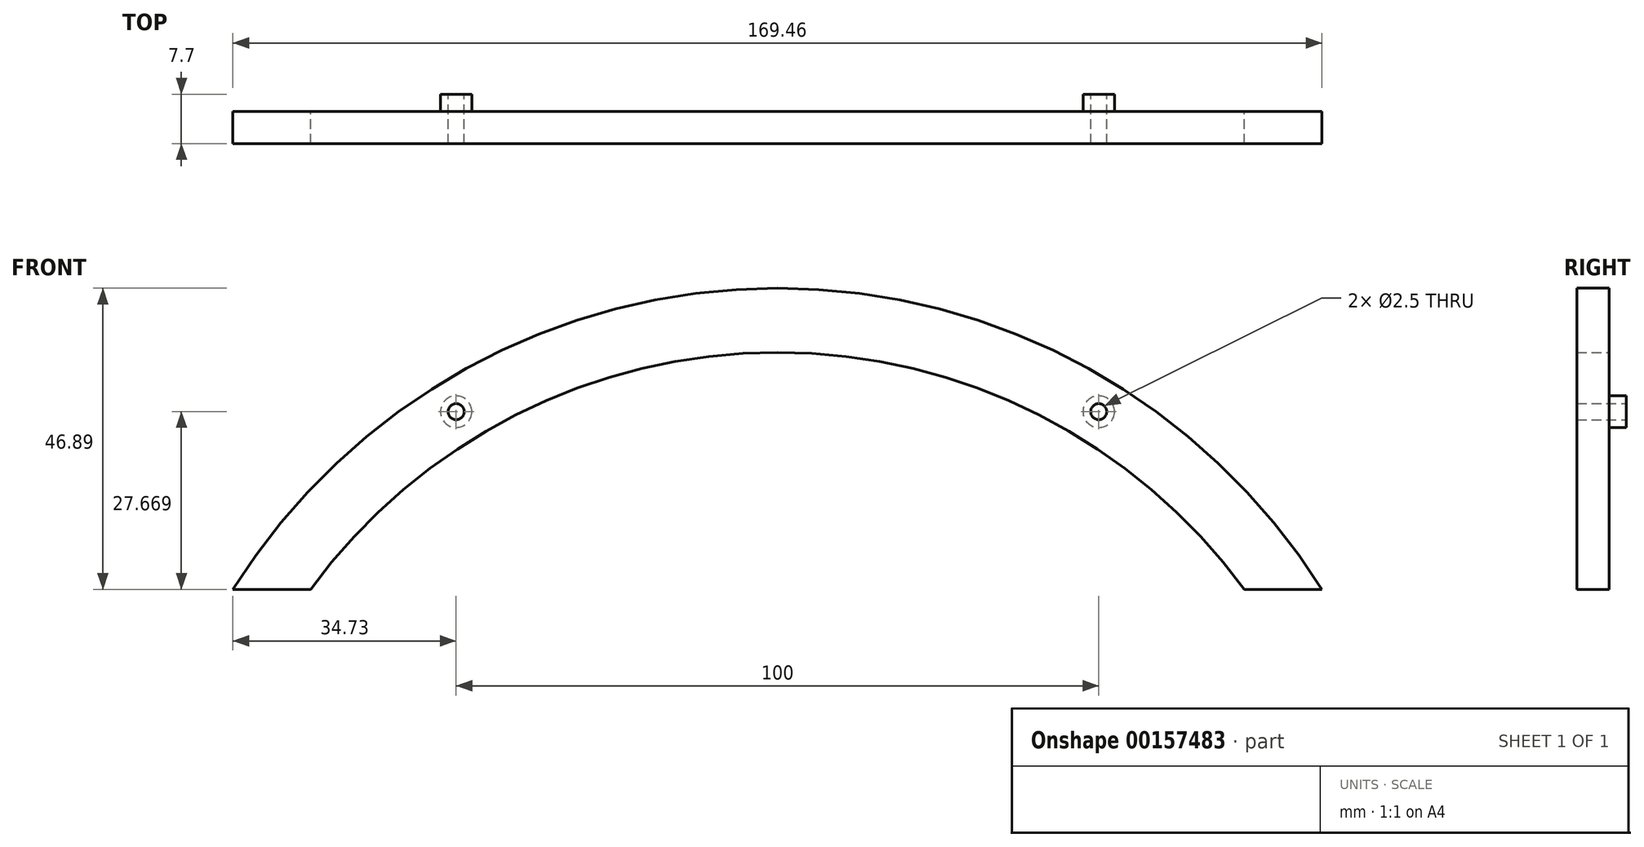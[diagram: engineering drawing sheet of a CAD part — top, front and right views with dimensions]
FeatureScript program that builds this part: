
annotation { "Feature Type Name" : "Feature", "Feature Type Description" : "" }
export const myFeature = defineFeature(function(context is Context, id is Id, definition is map)
    precondition{}
    {
        {
            var Q0;
            Q0=qCreatedBy(makeId("Front.planeOp"),FACE);
            var sketch = newSketch(context, id + "F0", { "sketchPlane" : qUnion([Q0])});
            skCircle(sketch, "E0", {"center": v(0, 100) * mm, "radius": 100 * mm});
            skCircle(sketch, "E1", {"center": v(50, 7.67) * mm, "radius": 5 * mm});
            skCircle(sketch, "E2", {"center": v(-50, 7.67) * mm, "radius": 5 * mm});
            skCircle(sketch, "E3", {"center": v(0, -73.1) * mm, "radius": 100 * mm});
            skCircle(sketch, "E4", {"center": v(0, -73.1) * mm, "radius": 90 * mm});
            skLineSegment(sketch, "E5", {"start": v(-110.96, -20) * mm, "end": v(122.03, -20) * mm});
            skCircle(sketch, "E6", {"center": v(-50, 7.67) * mm, "radius": 2.45 * mm});
            skCircle(sketch, "E7", {"center": v(50, 7.67) * mm, "radius": 2.45 * mm});
            skCircle(sketch, "E8", {"center": v(50, 7.67) * mm, "radius": 1.25 * mm});
            skCircle(sketch, "E9", {"center": v(-50, 7.67) * mm, "radius": 1.25 * mm});
            skSolve(sketch);
        }
        {
            var Q0;
            {var subQ0=sQuery(id+"F0.wireOp",EDGE,"E3");var subQ1=sQuery(id+"F0.wireOp",EDGE,"E0");var subQ6=makeQuery(id+"F0.imprint","INTERSECT",VERTEX,{"disambiguationData":[OD(0.0)],"derivedFrom":[subQ1,subQ0]});Q0=makeQuery(id+"F0.imprint","IMPRINT",FACE,{"disambiguationData":[TD([[makeQuery(id+"F0.imprint","IMPRINT",EDGE,{"disambiguationData":[TD([[subQ6,-1.0]])],"derivedFrom":subQ1}),1.0]])]});}
            var Q1;
            {var subQ0=sQuery(id+"F0.wireOp",EDGE,"E2");var subQ1=sQuery(id+"F0.wireOp",EDGE,"E0");var subQ2=makeQuery(id+"F0.imprint","INTERSECT",VERTEX,{"derivedFrom":[subQ1,subQ0]});Q1=makeQuery(id+"F0.imprint","IMPRINT",FACE,{"disambiguationData":[TD([[makeQuery(id+"F0.imprint","IMPRINT",EDGE,{"disambiguationData":[TD([[subQ2,-1.0]])],"derivedFrom":subQ1}),-1.0]])]});}
            var Q2;
            {var subQ0=sQuery(id+"F0.wireOp",EDGE,"E3");var subQ1=sQuery(id+"F0.wireOp",EDGE,"E2");var subQ2=makeQuery(id+"F0.imprint","INTERSECT",VERTEX,{"derivedFrom":[subQ1,subQ0]});Q2=makeQuery(id+"F0.imprint","IMPRINT",FACE,{"disambiguationData":[TD([[makeQuery(id+"F0.imprint","IMPRINT",EDGE,{"disambiguationData":[TD([[subQ2,-1.0]])],"derivedFrom":subQ1}),-1.0]])]});}
            var Q3;
            Q3=makeQuery(id+"F0.imprint","IMPRINT",FACE,{"disambiguationData":[TD([[makeQuery(id+"F0.imprint","IMPRINT",EDGE,{"derivedFrom":sQuery(id+"F0.wireOp",EDGE,"E6")}),1.0]])]});
            var Q4;
            {var subQ0=sQuery(id+"F0.wireOp",EDGE,"E3");var subQ1=sQuery(id+"F0.wireOp",EDGE,"E0");var subQ2=makeQuery(id+"F0.imprint","INTERSECT",VERTEX,{"disambiguationData":[OD(0.0)],"derivedFrom":[subQ1,subQ0]});Q4=makeQuery(id+"F0.imprint","IMPRINT",FACE,{"disambiguationData":[TD([[makeQuery(id+"F0.imprint","IMPRINT",EDGE,{"disambiguationData":[TD([[subQ2,-1.0]])],"derivedFrom":subQ1}),-1.0]])]});}
            var Q5;
            Q5=makeQuery(id+"F0.imprint","IMPRINT",FACE,{"disambiguationData":[TD([[makeQuery(id+"F0.imprint","IMPRINT",EDGE,{"derivedFrom":sQuery(id+"F0.wireOp",EDGE,"E6")}),-1.0]])]});
            var Q6;
            {var subQ0=sQuery(id+"F0.wireOp",EDGE,"E3");var subQ1=sQuery(id+"F0.wireOp",EDGE,"E1");var subQ2=makeQuery(id+"F0.imprint","INTERSECT",VERTEX,{"derivedFrom":[subQ1,subQ0]});Q6=makeQuery(id+"F0.imprint","IMPRINT",FACE,{"disambiguationData":[TD([[makeQuery(id+"F0.imprint","IMPRINT",EDGE,{"disambiguationData":[TD([[subQ2,1.0]])],"derivedFrom":subQ1}),-1.0]])]});}
            var Q7;
            Q7=makeQuery(id+"F0.imprint","IMPRINT",FACE,{"disambiguationData":[TD([[makeQuery(id+"F0.imprint","IMPRINT",EDGE,{"derivedFrom":sQuery(id+"F0.wireOp",EDGE,"E7")}),-1.0]])]});
            var Q8;
            {var subQ0=sQuery(id+"F0.wireOp",EDGE,"E4");var subQ1=sQuery(id+"F0.wireOp",EDGE,"E0");var subQ2=makeQuery(id+"F0.imprint","INTERSECT",VERTEX,{"disambiguationData":[OD(1.0)],"derivedFrom":[subQ1,subQ0]});Q8=makeQuery(id+"F0.imprint","IMPRINT",FACE,{"disambiguationData":[TD([[makeQuery(id+"F0.imprint","IMPRINT",EDGE,{"disambiguationData":[TD([[subQ2,-1.0]])],"derivedFrom":subQ1}),-1.0]])]});}
            var Q9;
            Q9=makeQuery(id+"F0.imprint","IMPRINT",FACE,{"disambiguationData":[TD([[makeQuery(id+"F0.imprint","IMPRINT",EDGE,{"derivedFrom":sQuery(id+"F0.wireOp",EDGE,"E7")}),1.0]])]});
            var Q10;
            {var subQ0=sQuery(id+"F0.wireOp",EDGE,"E3");var subQ1=sQuery(id+"F0.wireOp",EDGE,"E0");var subQ2=makeQuery(id+"F0.imprint","INTERSECT",VERTEX,{"disambiguationData":[OD(1.0)],"derivedFrom":[subQ1,subQ0]});Q10=makeQuery(id+"F0.imprint","IMPRINT",FACE,{"disambiguationData":[TD([[makeQuery(id+"F0.imprint","IMPRINT",EDGE,{"disambiguationData":[TD([[subQ2,1.0]])],"derivedFrom":subQ1}),-1.0]])]});}
            extrude(context, id + "F1", {"entities" : qUnion([Q0, Q1, Q2, Q3, Q4, Q5, Q6, Q7, Q8, Q9, Q10]), "depth" : 5 * mm, "offsetDistance" : 25 * mm});
        }
        {
            var Q0;
            Q0=makeQuery(id+"F0.imprint","IMPRINT",FACE,{"disambiguationData":[TD([[makeQuery(id+"F0.imprint","IMPRINT",EDGE,{"derivedFrom":sQuery(id+"F0.wireOp",EDGE,"E7")}),1.0]])]});
            var Q1;
            Q1=makeQuery(id+"F0.imprint","IMPRINT",FACE,{"disambiguationData":[TD([[makeQuery(id+"F0.imprint","IMPRINT",EDGE,{"derivedFrom":sQuery(id+"F0.wireOp",EDGE,"E6")}),1.0]])]});
            extrude(context, id + "F2", {"entities" : qUnion([Q0, Q1]), "operationType" : NewBodyOperationType.ADD, "oppositeDirection" : true, "depth" : 2.7 * mm, "offsetDistance" : 25 * mm});
        }
    });
